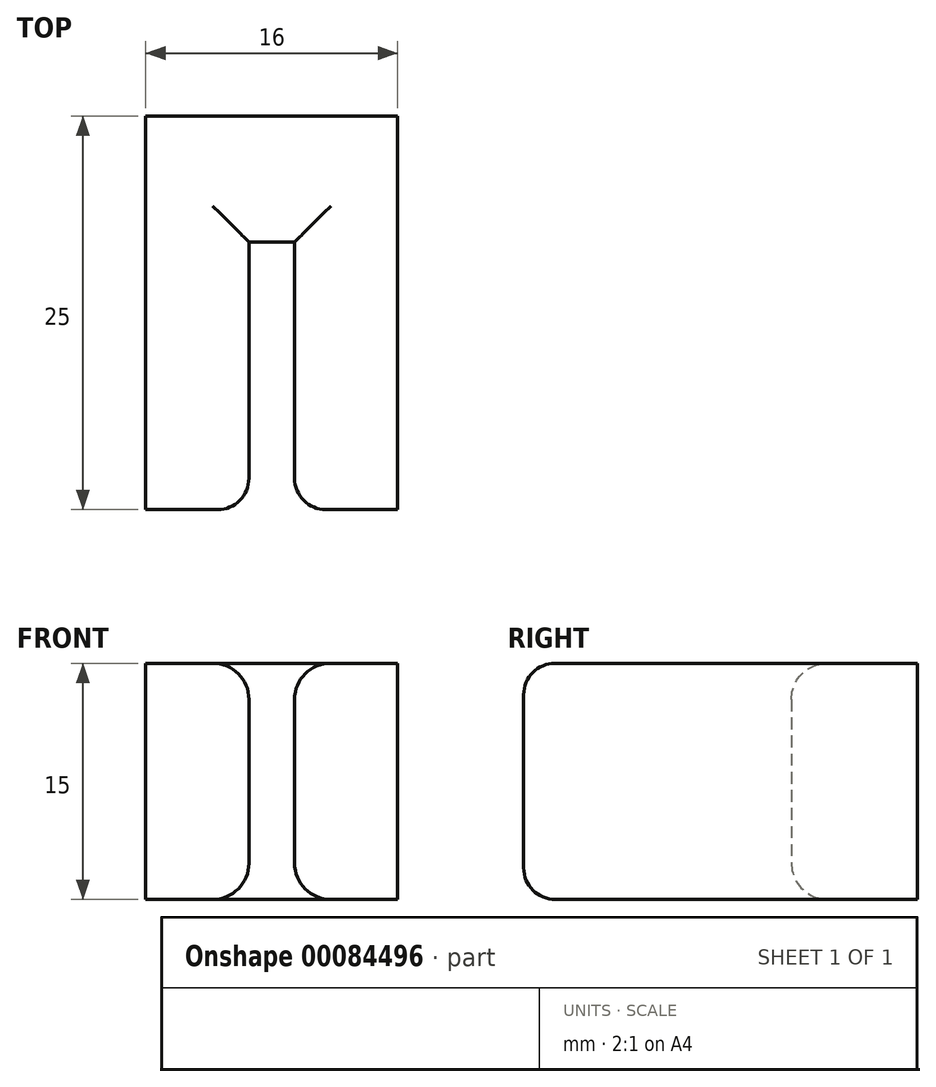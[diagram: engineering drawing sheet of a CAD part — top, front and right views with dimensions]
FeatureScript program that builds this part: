
annotation { "Feature Type Name" : "Feature", "Feature Type Description" : "" }
export const myFeature = defineFeature(function(context is Context, id is Id, definition is map)
    precondition{}
    {
        {
            var Q0;
            Q0=qCreatedBy(makeId("Top.planeOp"),FACE);
            var sketch = newSketch(context, id + "F0", { "sketchPlane" : qUnion([Q0])});
            skLineSegment(sketch, "E0.top", {"start": v(1.45, 8.5) * mm, "end": v(-1.45, 8.5) * mm});
            skLineSegment(sketch, "E0.left", {"start": v(1.45, -8.5) * mm, "end": v(1.45, 8.5) * mm});
            skLineSegment(sketch, "E0.right", {"start": v(-1.45, -8.5) * mm, "end": v(-1.45, 8.5) * mm});
            skPoint(sketch, "E0.middle", {"position": v(0, 0) * mm});
            skLineSegment(sketch, "E1.bottom", {"start": v(1.45, -8.5) * mm, "end": v(8, -8.5) * mm});
            skLineSegment(sketch, "E1.top", {"start": v(0, 16.5) * mm, "end": v(8, 16.5) * mm});
            skLineSegment(sketch, "E1.left", {"start": v(0, -8.5) * mm, "end": v(0, 16.5) * mm, "construction": true});
            skLineSegment(sketch, "E1.right", {"start": v(8, -8.5) * mm, "end": v(8, 16.5) * mm});
            skLineSegment(sketch, "E2.MirrorCS", {"start": v(0, 16.5) * mm, "end": v(-8, 16.5) * mm});
            skLineSegment(sketch, "E3.MirrorCS", {"start": v(-8, -8.5) * mm, "end": v(-8, 16.5) * mm});
            skLineSegment(sketch, "E4.MirrorCS", {"start": v(-1.45, -8.5) * mm, "end": v(-8, -8.5) * mm});
            skPoint(sketch, "E5.orphan", {"position": v(0, -8.5) * mm});
            skSolve(sketch);
        }
        {
            var Q0;
            Q0 = qSketchRegion(id + "F0", true);
            extrude(context, id + "F1", {"entities" : qUnion([Q0]), "depth" : 15 * mm});
        }
        {
            var Q0;
            Q0=makeQuery(id+"F1.opExtrude","CAP_EDGE",EDGE,{"disambiguationData":[OSD([sQuery(id+"F0.wireOp",EDGE,"E0.right")])],"isStart":false});
            var Q1;
            Q1=makeQuery(id+"F1.opExtrude","CAP_EDGE",EDGE,{"disambiguationData":[OSD([sQuery(id+"F0.wireOp",EDGE,"E0.top")])],"isStart":false});
            var Q2;
            Q2=makeQuery(id+"F1.opExtrude","CAP_EDGE",EDGE,{"disambiguationData":[OSD([sQuery(id+"F0.wireOp",EDGE,"E0.left")])],"isStart":false});
            var Q3;
            Q3=makeQuery(id+"F1.opExtrude","CAP_EDGE",EDGE,{"disambiguationData":[OSD([sQuery(id+"F0.wireOp",EDGE,"E0.left")])],"isStart":true});
            var Q4;
            Q4=makeQuery(id+"F1.opExtrude","CAP_EDGE",EDGE,{"disambiguationData":[OSD([sQuery(id+"F0.wireOp",EDGE,"E0.top")])],"isStart":true});
            var Q5;
            Q5=makeQuery(id+"F1.opExtrude","CAP_EDGE",EDGE,{"disambiguationData":[OSD([sQuery(id+"F0.wireOp",EDGE,"E0.right")])],"isStart":true});
            fillet(context, id + "F2", {"entities" : qUnion([Q0, Q1, Q2, Q3, Q4, Q5]), "radius" : 2.3 * mm, "tangentPropagation" : true, "allowEdgeOverflow" : false});
        }
        {
            var Q0;
            Q0=makeQuery(id+"F1.opExtrude","CAP_EDGE",EDGE,{"disambiguationData":[OSD([sQuery(id+"F0.wireOp",EDGE,"E4.MirrorCS")])],"isStart":false});
            var Q1;
            Q1=makeQuery(id+"F1.opExtrude","CAP_EDGE",EDGE,{"disambiguationData":[OSD([sQuery(id+"F0.wireOp",EDGE,"E1.bottom")])],"isStart":false});
            fillet(context, id + "F3", {"entities" : qUnion([Q0, Q1]), "radius" : 2 * mm, "tangentPropagation" : true, "allowEdgeOverflow" : false});
        }
    });
